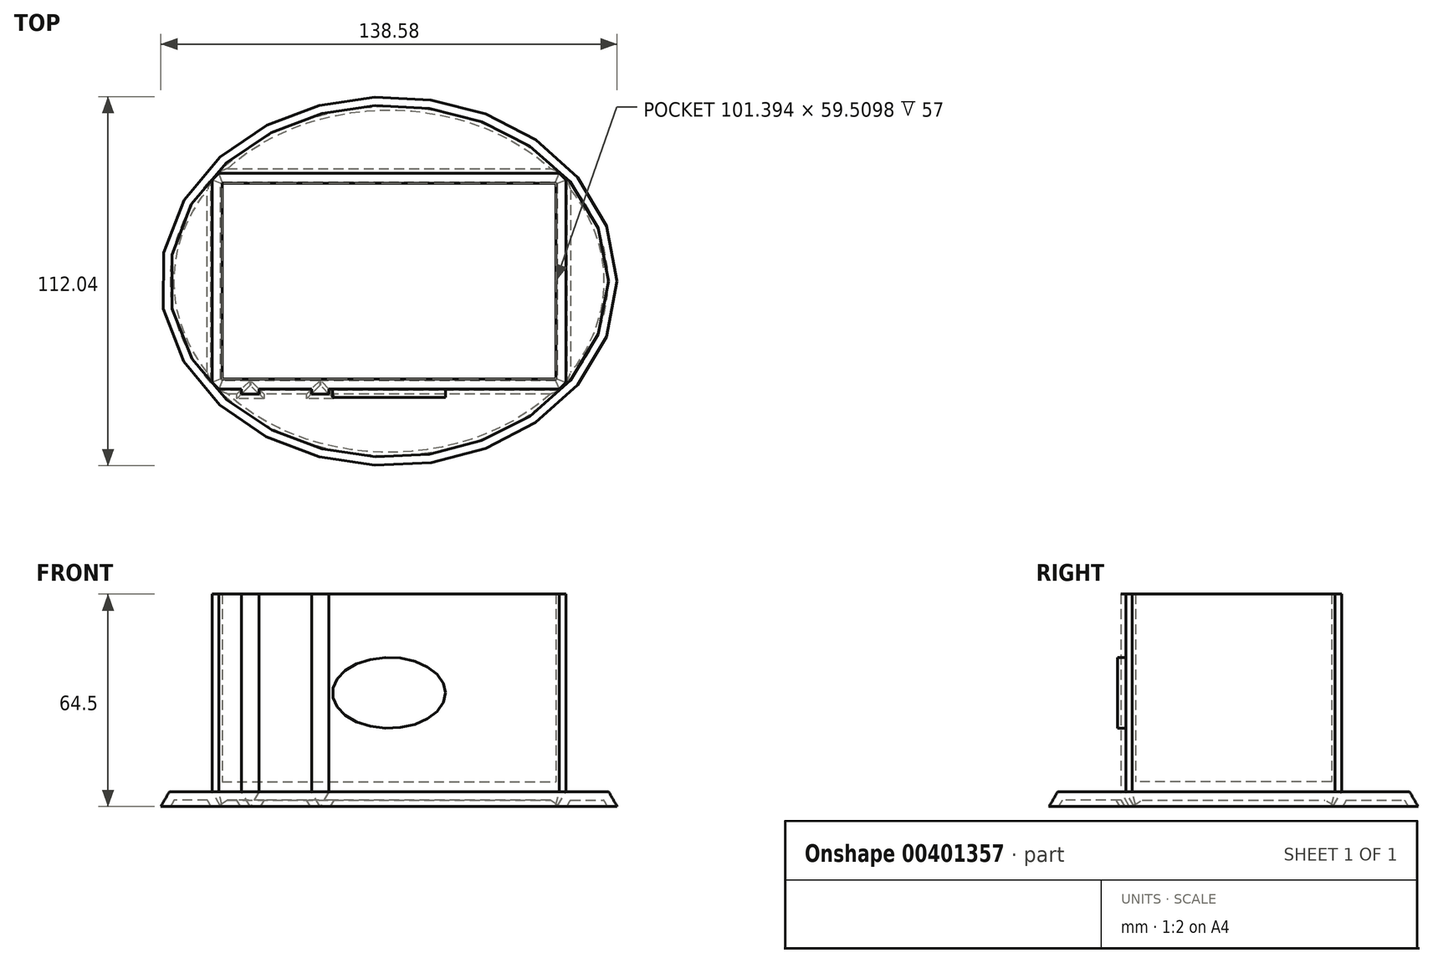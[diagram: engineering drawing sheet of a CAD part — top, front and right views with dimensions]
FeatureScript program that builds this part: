
annotation { "Feature Type Name" : "Feature", "Feature Type Description" : "" }
export const myFeature = defineFeature(function(context is Context, id is Id, definition is map)
    precondition{}
    {
        {
            var Q0;
            Q0=qCreatedBy(makeId("Top.planeOp"),FACE);
            var sketch = newSketch(context, id + "F0", { "sketchPlane" : qUnion([Q0])});
            skLineSegment(sketch, "E0.top", {"start": v(0, 32.75) * mm, "end": v(53.7, 32.75) * mm});
            skLineSegment(sketch, "E0.right", {"start": v(53.7, 0) * mm, "end": v(53.7, 32.75) * mm});
            skLineSegment(sketch, "E1.MirrorCS", {"start": v(0, 32.75) * mm, "end": v(-53.7, 32.75) * mm});
            skLineSegment(sketch, "E2.MirrorCS", {"start": v(-53.7, 0) * mm, "end": v(-53.7, 32.75) * mm});
            skLineSegment(sketch, "E3.MirrorCS", {"start": v(0, -32.75) * mm, "end": v(53.7, -32.75) * mm});
            skLineSegment(sketch, "E4.MirrorCS", {"start": v(53.7, 0) * mm, "end": v(53.7, -32.75) * mm});
            skLineSegment(sketch, "E5.MirrorCS", {"start": v(-53.7, 0) * mm, "end": v(-53.7, -32.75) * mm});
            skLineSegment(sketch, "E6.MirrorCS", {"start": v(0, -32.75) * mm, "end": v(-53.7, -32.75) * mm});
            skSolve(sketch);
        }
        {
            var Q0;
            Q0=makeQuery(id+"F0.imprint","IMPRINT",FACE,{"disambiguationData":[TD([[makeQuery(id+"F0.imprint","IMPRINT",EDGE,{"derivedFrom":sQuery(id+"F0.wireOp",EDGE,"E0.right")}),1.0]])]});
            extrude(context, id + "F1", {"entities" : qUnion([Q0]), "endBound" : BoundingType.SYMMETRIC, "depth" : 60 * mm});
        }
        {
            var Q0;
            Q0=makeQuery(id+"F1.opExtrude","CAP_FACE",FACE,{"disambiguationData":[OSD([sQuery(id+"F0.wireOp",EDGE,"E0.right"),sQuery(id+"F0.wireOp",EDGE,"E1.MirrorCS"),sQuery(id+"F0.wireOp",EDGE,"E2.MirrorCS"),sQuery(id+"F0.wireOp",EDGE,"E0.top"),sQuery(id+"F0.wireOp",EDGE,"E3.MirrorCS"),sQuery(id+"F0.wireOp",EDGE,"E4.MirrorCS"),sQuery(id+"F0.wireOp",EDGE,"E5.MirrorCS"),sQuery(id+"F0.wireOp",EDGE,"E6.MirrorCS")])],"isStart":false});
            shell(context, id + "F2", {"entities" : qUnion([Q0]), "thickness" : 3 * mm});
        }
        {
            var Q0;
            Q0=makeQuery(id+"F1.opExtrude","SWEPT_EDGE",EDGE,{"disambiguationData":[OSD([sQuery(id+"F0.wireOp",EDGE,"E3.MirrorCS"),sQuery(id+"F0.wireOp",EDGE,"E4.MirrorCS")])]});
            var Q1;
            Q1=makeQuery(id+"F1.opExtrude","SWEPT_EDGE",EDGE,{"disambiguationData":[OSD([sQuery(id+"F0.wireOp",EDGE,"E1.MirrorCS"),sQuery(id+"F0.wireOp",EDGE,"E2.MirrorCS")])]});
            var Q2;
            Q2=makeQuery(id+"F1.opExtrude","SWEPT_EDGE",EDGE,{"disambiguationData":[OSD([sQuery(id+"F0.wireOp",EDGE,"E0.right"),sQuery(id+"F0.wireOp",EDGE,"E0.top")])]});
            var Q3;
            Q3=makeQuery(id+"F1.opExtrude","SWEPT_EDGE",EDGE,{"disambiguationData":[OSD([sQuery(id+"F0.wireOp",EDGE,"E5.MirrorCS"),sQuery(id+"F0.wireOp",EDGE,"E6.MirrorCS")])]});
            chamfer(context, id + "F3", {"entities" : qUnion([Q0, Q1, Q2, Q3]), "width" : 2 * mm, "tangentPropagation" : true});
        }
        {
            var Q0;
            Q0=makeQuery(id+"F1.opExtrude","SWEPT_FACE",FACE,{"disambiguationData":[OSD([sQuery(id+"F0.wireOp",EDGE,"E3.MirrorCS"),sQuery(id+"F0.wireOp",EDGE,"E6.MirrorCS")])]});
            var sketch = newSketch(context, id + "F4", { "sketchPlane" : qUnion([Q0])});
            skLineSegment(sketch, "E7.bottom", {"start": v(-39.47, 30) * mm, "end": v(-34.16, 30) * mm});
            skLineSegment(sketch, "E7.top", {"start": v(-39.47, -30) * mm, "end": v(-34.16, -30) * mm});
            skLineSegment(sketch, "E7.left", {"start": v(-39.47, 30) * mm, "end": v(-39.47, -30) * mm});
            skLineSegment(sketch, "E7.right", {"start": v(-34.16, 30) * mm, "end": v(-34.16, -30) * mm});
            skLineSegment(sketch, "E8.MirrorCS", {"start": v(-44.78, 30) * mm, "end": v(-44.78, -30) * mm});
            skLineSegment(sketch, "E9.MirrorCS", {"start": v(-34.16, 40) * mm, "end": v(-34.16, -40) * mm});
            skLineSegment(sketch, "E10.MirrorCS", {"start": v(-28.85, 30) * mm, "end": v(-28.85, -30) * mm});
            skLineSegment(sketch, "E11.MirrorCS", {"start": v(-28.85, 40) * mm, "end": v(-28.85, -40) * mm});
            skLineSegment(sketch, "E12.MirrorCS", {"start": v(-23.54, 40) * mm, "end": v(-23.54, -40) * mm});
            skLineSegment(sketch, "E13.MirrorCS", {"start": v(-18.23, 40) * mm, "end": v(-18.23, -40) * mm});
            skSolve(sketch);
        }
        {
            var Q0;
            {var subQ0=sQuery(id+"F4.wireOp",EDGE,"E8.MirrorCS");Q0=makeQuery(id+"F4.imprint","IMPRINT",FACE,{"disambiguationData":[TD([[makeQuery(id+"F4.imprint","IMPRINT",EDGE,{"derivedFrom":subQ0}),1.0]])]});}
            var Q1;
            {var subQ0=sQuery(id+"F4.wireOp",EDGE,"E11.MirrorCS");Q1=makeQuery(id+"F4.imprint","IMPRINT",FACE,{"disambiguationData":[TD([[makeQuery(id+"F4.imprint","IMPRINT",EDGE,{"derivedFrom":subQ0}),-1.0]])]});}
            var Q2;
            {var subQ0=sQuery(id+"F4.wireOp",EDGE,"E13.MirrorCS");Q2=makeQuery(id+"F4.imprint","IMPRINT",FACE,{"disambiguationData":[TD([[makeQuery(id+"F4.imprint","IMPRINT",EDGE,{"derivedFrom":subQ0}),-1.0]])]});}
            var Q3;
            Q3=sQuery(id+"F4.wireOp",EDGE,"E13.MirrorCS");
            var Q4;
            Q4=sQuery(id+"F4.wireOp",EDGE,"E8.MirrorCS");
            var Q5;
            Q5=sQuery(id+"F4.wireOp",EDGE,"E12.MirrorCS");
            var Q6;
            Q6=sQuery(id+"F4.wireOp",EDGE,"E7.left");
            var Q7;
            Q7=sQuery(id+"F4.wireOp",EDGE,"E9.MirrorCS");
            var Q8;
            Q8=sQuery(id+"F4.wireOp",EDGE,"E11.MirrorCS");
            extrude(context, id + "F5", {"entities" : qUnion([Q0, Q1, Q2]), "operationType" : NewBodyOperationType.ADD, "surfaceEntities" : qUnion([Q3, Q4, Q5, Q6, Q7, Q8]), "depth" : 1.5 * mm});
        }
        {
            var Q0;
            {var subQ0=sQuery(id+"F4.wireOp",EDGE,"E13.MirrorCS");var subQ1=sQuery(id+"F0.wireOp",EDGE,"E6.MirrorCS");var subQ2=sQuery(id+"F0.wireOp",EDGE,"E3.MirrorCS");var subQ30=makeQuery(id+"F5.opExtrude","SWEPT_FACE",FACE,{"disambiguationData":[OSD([subQ0])]});Q0=makeQuery(id+"F9F7dy0vkw7aQIL_1.1.F5.boolean.opBoolean","SPLIT",FACE,{"disambiguationData":[TD([subQ30])],"derivedFrom":makeQuery(id+"F5.boolean.opBoolean","SPLIT",FACE,{"disambiguationData":[TD([subQ30])],"derivedFrom":makeQuery(id+"F1.opExtrude","SWEPT_FACE",FACE,{"disambiguationData":[OSD([subQ2,subQ1])]})})});}
            var sketch = newSketch(context, id + "F6", { "sketchPlane" : qUnion([Q0])});
            skEllipse(sketch, "E14", {"center": v(0, 0) * mm, "majorRadius": 17.12 * mm, "minorRadius": 10.76 * mm, "majorAxis": v(1, 0)});
            skSolve(sketch);
        }
        {
            var Q0;
            Q0=makeQuery(id+"F6.imprint","IMPRINT",FACE,{"disambiguationData":[TD([[makeQuery(id+"F6.imprint","IMPRINT",EDGE,{"derivedFrom":sQuery(id+"F6.wireOp",EDGE,"E14")}),1.0]])]});
            var Q1;
            Q1=sQuery(id+"F6.wireOp",EDGE,"E14");
            extrude(context, id + "F7", {"entities" : qUnion([Q0]), "operationType" : NewBodyOperationType.ADD, "surfaceEntities" : qUnion([Q1]), "depth" : 2.5 * mm});
        }
        {
            var Q0;
            {var subQ0=sQuery(id+"F0.wireOp",EDGE,"E6.MirrorCS");var subQ1=sQuery(id+"F0.wireOp",EDGE,"E3.MirrorCS");var subQ2=makeQuery(id+"F1.opExtrude","CAP_EDGE",EDGE,{"disambiguationData":[OSD([subQ1,subQ0])],"isStart":true});var subQ3=makeQuery(id+"F4.imprint","IMPRINT",EDGE,{"disambiguationData":[TD([[makeQuery(id+"F4.imprint","INTERSECT",VERTEX,{"derivedFrom":[subQ2,sQuery(id+"F4.wireOp",EDGE,"E13.MirrorCS")]}),-1.0]])],"derivedFrom":subQ2});var subQ5=makeQuery(id+"F4.imprint","IMPRINT",EDGE,{"disambiguationData":[TD([[makeQuery(id+"F4.imprint","INTERSECT",VERTEX,{"derivedFrom":[subQ2,sQuery(id+"F4.wireOp",EDGE,"E11.MirrorCS")]}),-1.0]])],"derivedFrom":subQ2});var subQ6=makeQuery(id+"F4.imprint","IMPRINT",EDGE,{"disambiguationData":[TD([[makeQuery(id+"F4.imprint","INTERSECT",VERTEX,{"derivedFrom":[subQ2,sQuery(id+"F4.wireOp",EDGE,"E8.MirrorCS")]}),1.0]])],"derivedFrom":subQ2});Q0=makeQuery(id+"F9F7dy0vkw7aQIL_1.1.F5.boolean.opBoolean","MERGE",FACE,{"derivedFrom":[makeQuery(id+"F5.boolean.opBoolean","MERGE",FACE,{"derivedFrom":[makeQuery(id+"F1.opExtrude","CAP_FACE",FACE,{"disambiguationData":[OSD([sQuery(id+"F0.wireOp",EDGE,"E0.right"),sQuery(id+"F0.wireOp",EDGE,"E1.MirrorCS"),sQuery(id+"F0.wireOp",EDGE,"E2.MirrorCS"),sQuery(id+"F0.wireOp",EDGE,"E0.top"),subQ1,sQuery(id+"F0.wireOp",EDGE,"E4.MirrorCS"),sQuery(id+"F0.wireOp",EDGE,"E5.MirrorCS"),subQ0])],"isStart":true}),makeQuery(id+"F5.opExtrude","SWEPT_FACE",FACE,{"disambiguationData":[OSD([subQ1,subQ0]),TDD([subQ6])]}),makeQuery(id+"F5.opExtrude","SWEPT_FACE",FACE,{"disambiguationData":[OSD([subQ1,subQ0]),TDD([subQ5])]}),makeQuery(id+"F5.opExtrude","SWEPT_FACE",FACE,{"disambiguationData":[OSD([subQ1,subQ0]),TDD([subQ3])]})]}),makeQuery(id+"F9F7dy0vkw7aQIL_1.1.F5.opExtrude","SWEPT_FACE",FACE,{"disambiguationData":[OSD([subQ1,subQ0]),TDD([subQ6])]}),makeQuery(id+"F9F7dy0vkw7aQIL_1.1.F5.opExtrude","SWEPT_FACE",FACE,{"disambiguationData":[OSD([subQ1,subQ0]),TDD([subQ5])]}),makeQuery(id+"F9F7dy0vkw7aQIL_1.1.F5.opExtrude","SWEPT_FACE",FACE,{"disambiguationData":[OSD([subQ1,subQ0]),TDD([subQ3])]})]});}
            var sketch = newSketch(context, id + "F8", { "sketchPlane" : qUnion([Q0])});
            skSolve(sketch);
        }
        {
            var Q0;
            {var subQ12=sQuery(id+"F0.wireOp",EDGE,"E4.MirrorCS");var subQ16=sQuery(id+"F0.wireOp",EDGE,"E0.right");Q0=makeQuery(id+"F8.imprint","IMPRINT",FACE,{"disambiguationData":[TD([[makeQuery(id+"F8.imprint","IMPRINT",EDGE,{"derivedFrom":makeQuery(id+"F1.opExtrude","CAP_EDGE",EDGE,{"disambiguationData":[OSD([subQ16,subQ12])],"isStart":true})}),1.0]])]});}
            var sketch = newSketch(context, id + "F9", { "sketchPlane" : qUnion([Q0])});
            skEllipse(sketch, "E15", {"center": v(0, 0) * mm, "majorRadius": 66.7 * mm, "minorRadius": 53.42 * mm, "majorAxis": v(-1, 0)});
            skSolve(sketch);
        }
        {
            var Q0;
            Q0=makeQuery(id+"F9.imprint","IMPRINT",FACE,{"disambiguationData":[TD([[makeQuery(id+"F9.imprint","IMPRINT",EDGE,{"derivedFrom":sQuery(id+"F9.wireOp",EDGE,"E15")}),1.0]])]});
            cPlane(context, id + "F10", {"entities" : qUnion([Q0]), "cplaneType" : CPlaneType.OFFSET, "offset" : 4.5 * mm, "width" : 152.4 * mm, "height" : 152.4 * mm});
        }
        {
            var Q0;
            Q0=makeQuery(id+"F9.imprint","IMPRINT",FACE,{"disambiguationData":[TD([[makeQuery(id+"F9.imprint","IMPRINT",EDGE,{"derivedFrom":sQuery(id+"F9.wireOp",EDGE,"E15")}),1.0]])]});
            var Q1;
            Q1=sQuery(id+"F9.wireOp",EDGE,"E15");
            extrude(context, id + "F11", {"entities" : qUnion([Q0]), "surfaceEntities" : qUnion([Q1]), "depth" : 4.5 * mm, "hasDraft" : true, "draftAngle" : 30 * degree});
        }
        {
            var Q0;
            Q0=makeQuery(id+"F11.opExtrude","CAP_FACE",FACE,{"disambiguationData":[OSD([sQuery(id+"F0.wireOp",EDGE,"E0.right"),sQuery(id+"F0.wireOp",EDGE,"E1.MirrorCS"),sQuery(id+"F0.wireOp",EDGE,"E2.MirrorCS"),sQuery(id+"F0.wireOp",EDGE,"E0.top"),sQuery(id+"F0.wireOp",EDGE,"E3.MirrorCS"),sQuery(id+"F0.wireOp",EDGE,"E4.MirrorCS"),sQuery(id+"F0.wireOp",EDGE,"E5.MirrorCS"),sQuery(id+"F0.wireOp",EDGE,"E6.MirrorCS"),sQuery(id+"F4.wireOp",EDGE,"E7.top"),sQuery(id+"F4.wireOp",EDGE,"E8.MirrorCS"),sQuery(id+"F4.wireOp",EDGE,"E7.left"),sQuery(id+"F4.wireOp",EDGE,"E11.MirrorCS"),sQuery(id+"F4.wireOp",EDGE,"E9.MirrorCS"),sQuery(id+"F4.wireOp",EDGE,"E13.MirrorCS"),sQuery(id+"F4.wireOp",EDGE,"E12.MirrorCS"),sQuery(id+"F9.wireOp",EDGE,"E15")])],"isStart":false});
            shell(context, id + "F12", {"entities" : qUnion([Q0]), "thickness" : 2.54 * mm});
        }
    });
